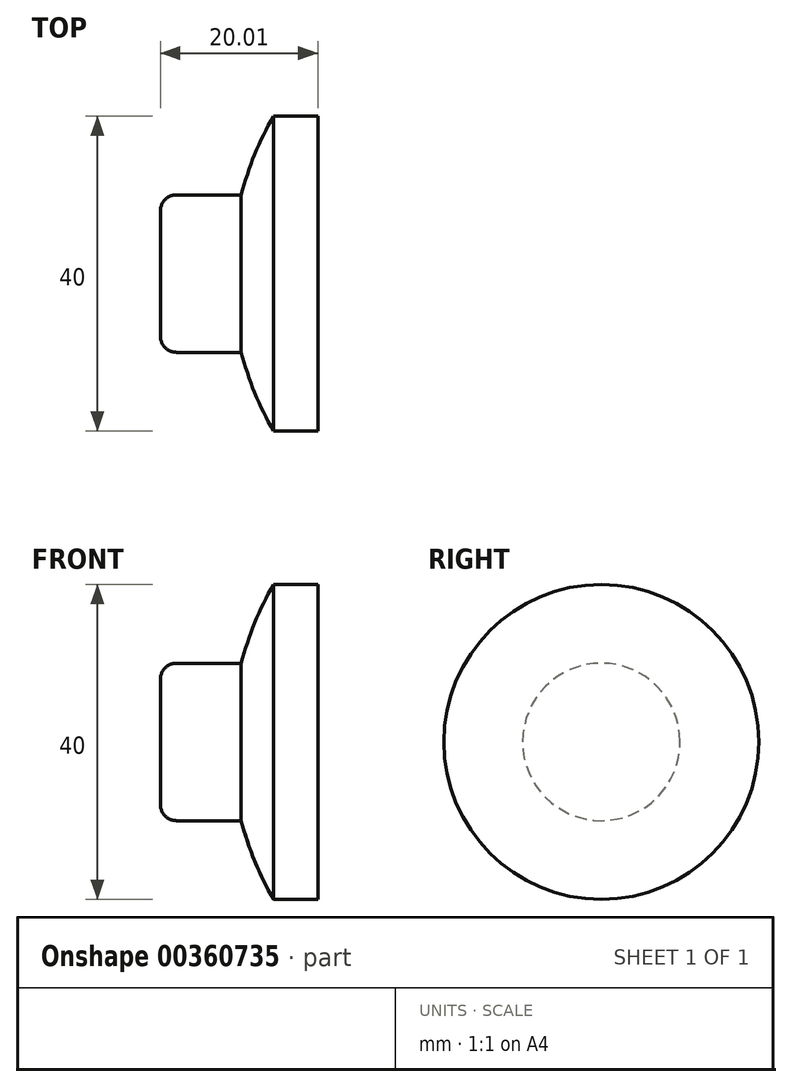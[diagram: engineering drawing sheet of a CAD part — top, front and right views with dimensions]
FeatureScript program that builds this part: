
annotation { "Feature Type Name" : "Feature", "Feature Type Description" : "" }
export const myFeature = defineFeature(function(context is Context, id is Id, definition is map)
    precondition{}
    {
        {
            var Q0;
            Q0=qCreatedBy(makeId("Front.planeOp"),FACE);
            var sketch = newSketch(context, id + "F0", { "sketchPlane" : qUnion([Q0])});
            skArc(sketch, "E0", {"start": v(-40, 0) * mm, "mid": v(-38.64, 10.35) * mm, "end": v(-34.65, 20) * mm});
            skLineSegment(sketch, "E1", {"start": v(-34.65, 20) * mm, "end": v(-29, 20) * mm});
            skLineSegment(sketch, "E2", {"start": v(-29, 20) * mm, "end": v(-29, 0) * mm});
            skLineSegment(sketch, "E3", {"start": v(-29, 0) * mm, "end": v(-49, 0) * mm});
            skLineSegment(sketch, "E4", {"start": v(-45.83, 10) * mm, "end": v(-38.73, 10) * mm});
            skLineSegment(sketch, "E5", {"start": v(-49, 0) * mm, "end": v(-49, 10) * mm});
            skLineSegment(sketch, "E6", {"start": v(-45.83, 10) * mm, "end": v(-49, 10) * mm});
            skSolve(sketch);
        }
        {
            var Q0;
            {var subQ1=sQuery(id+"F0.wireOp",EDGE,"E4");Q0=makeQuery(id+"F0.imprint","IMPRINT",FACE,{"disambiguationData":[TD([[makeQuery(id+"F0.imprint","IMPRINT",EDGE,{"derivedFrom":subQ1}),-1.0]])]});}
            var Q1;
            {var subQ1=sQuery(id+"F0.wireOp",EDGE,"E1");Q1=makeQuery(id+"F0.imprint","IMPRINT",FACE,{"disambiguationData":[TD([[makeQuery(id+"F0.imprint","IMPRINT",EDGE,{"derivedFrom":subQ1}),-1.0]])]});}
            var Q2;
            Q2=sQuery(id+"F0.wireOp",EDGE,"E3");
            revolve(context, id + "F1", {"entities" : qUnion([Q0, Q1]), "axis" : qUnion([Q2]), "revolveType" : RevolveType.FULL});
        }
        {
            var Q0;
            Q0=makeQuery(id+"F1.opRevolve","SWEPT_EDGE",EDGE,{"disambiguationData":[OSD([sQuery(id+"F0.wireOp",EDGE,"E5"),sQuery(id+"F0.wireOp",EDGE,"E6")])]});
            fillet(context, id + "F2", {"entities" : qUnion([Q0]), "radius" : 2.03 * mm, "tangentPropagation" : true, "allowEdgeOverflow" : false});
        }
    });
